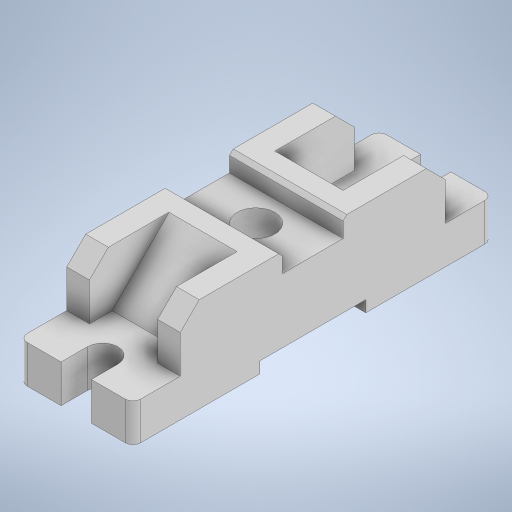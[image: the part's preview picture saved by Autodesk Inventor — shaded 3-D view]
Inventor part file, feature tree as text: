
AUTODESK INVENTOR PART (.ipt)
format: ipt  version: 2023 (Build 270158000, 158)  size: 325,120 bytes
history: native  units: mm
features: chamfer x6, extrude x4, sketch x1, fillet x1
ambient origin geometry x8: Origin, YZ Plane, XZ Plane, XY Plane, X Axis, Y Axis, Z Axis, Center Point
bodies: Solido1 (feature_tree)
feature tree (12):
  sketch  "Schizzo1"
  extrude  "Estrusione1"  Depth=15.0mm
  extrude  "Estrusione2"  Depth=47.5mm
  extrude  "Estrusione3"  Depth=11.0mm
  extrude  "Estrusione4"  Depth=5.0mm
  chamfer  "Smusso1"  Distance=8.0mm
  chamfer  "Smusso2"  Distance=14.0mm
  chamfer  "Smusso3"  Distance=6.0mm
  chamfer  "Smusso4"  Distance=10.0mm
  fillet  "Raccordo1"  Radius=25.0mm
  chamfer  "Smusso5"  Distance=20.0mm
  chamfer  "Smusso6"  Distance=3.0mm
